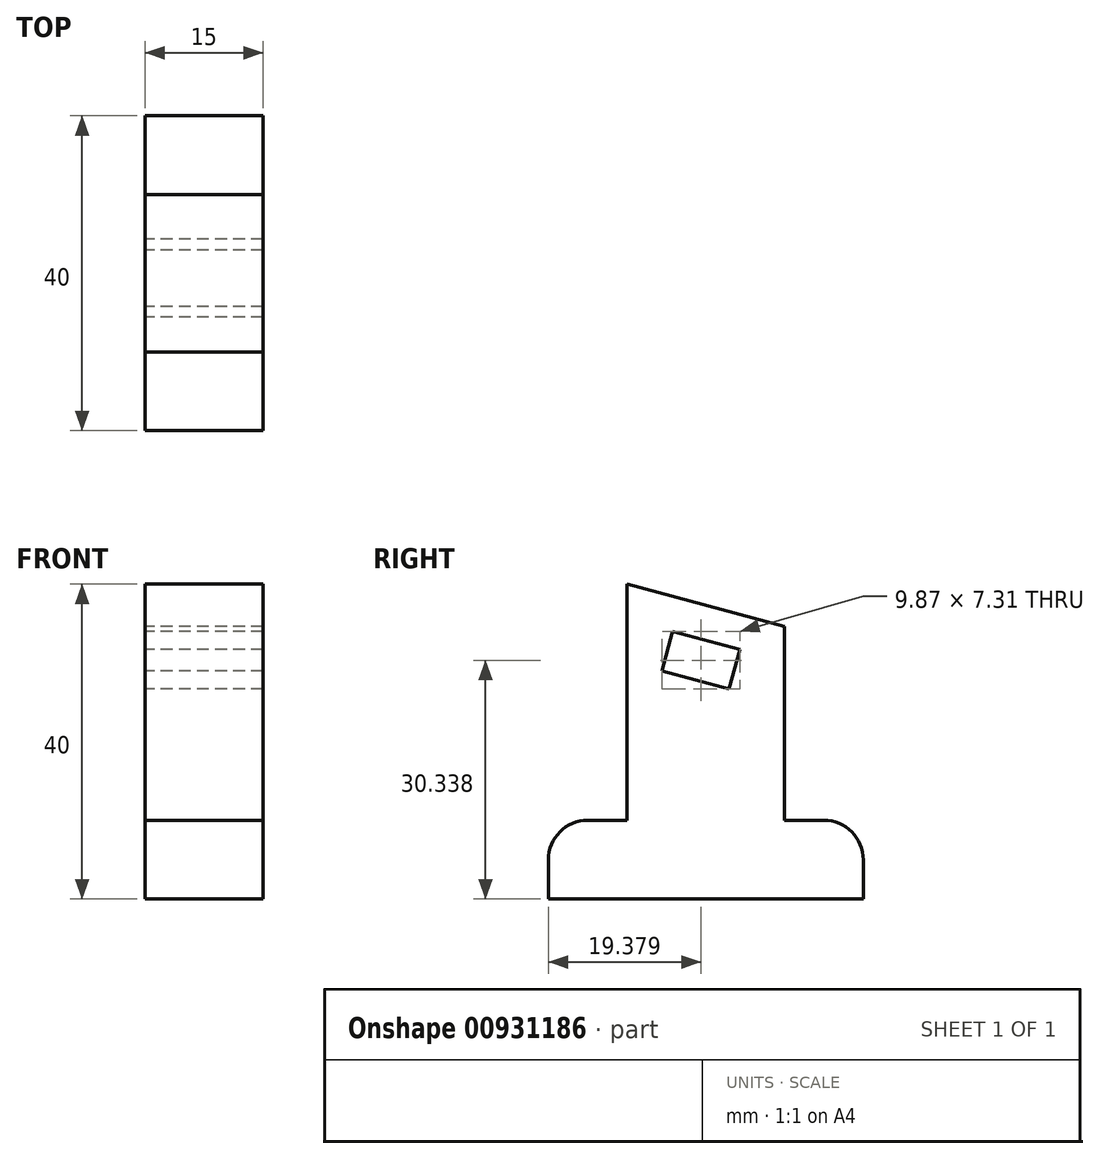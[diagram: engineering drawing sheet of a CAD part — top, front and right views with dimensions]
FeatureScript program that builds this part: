
annotation { "Feature Type Name" : "Feature", "Feature Type Description" : "" }
export const myFeature = defineFeature(function(context is Context, id is Id, definition is map)
    precondition{}
    {
        {
            var Q0;
            Q0=qCreatedBy(makeId("Right.planeOp"),FACE);
            var sketch = newSketch(context, id + "F0", { "sketchPlane" : qUnion([Q0])});
            skLineSegment(sketch, "E0.top", {"start": v(-10, -20) * mm, "end": v(10, -20) * mm});
            skLineSegment(sketch, "E0.left", {"start": v(-10, 20) * mm, "end": v(-10, -10) * mm});
            skLineSegment(sketch, "E0.right", {"start": v(10, 14.64) * mm, "end": v(10, -10) * mm});
            skPoint(sketch, "E0.middle", {"position": v(0, 0) * mm});
            skLineSegment(sketch, "E1.bottom", {"start": v(10, -20) * mm, "end": v(20, -20) * mm});
            skLineSegment(sketch, "E1.top", {"start": v(10, -10) * mm, "end": v(15, -10) * mm});
            skLineSegment(sketch, "E1.right", {"start": v(20, -20) * mm, "end": v(20, -15) * mm});
            skLineSegment(sketch, "E2.MirrorCS", {"start": v(-20, -20) * mm, "end": v(-20, -15) * mm});
            skLineSegment(sketch, "E3.MirrorCS", {"start": v(-10, -20) * mm, "end": v(-20, -20) * mm});
            skLineSegment(sketch, "E4.MirrorCS", {"start": v(-10, -10) * mm, "end": v(-15, -10) * mm});
            skPoint(sketch, "E5.orphan", {"position": v(0, -20) * mm});
            skPoint(sketch, "E6.start.orphan", {"position": v(0, 20) * mm});
            skLineSegment(sketch, "E7", {"start": v(-10, 20) * mm, "end": v(10, 14.64) * mm});
            skPoint(sketch, "E8.orphan", {"position": v(10, 20) * mm});
            skLineSegment(sketch, "E9", {"start": v(4.31, 11.7) * mm, "end": v(-4.21, 14) * mm});
            skLineSegment(sketch, "E10", {"start": v(-4.21, 14) * mm, "end": v(-5.56, 8.97) * mm});
            skLineSegment(sketch, "E11", {"start": v(-5.56, 8.97) * mm, "end": v(2.97, 6.68) * mm});
            skLineSegment(sketch, "E12", {"start": v(2.97, 6.68) * mm, "end": v(4.31, 11.7) * mm});
            skPoint(sketch, "E13.visualSharp", {"position": v(-20, -10) * mm});
            skArc(sketch, "E13.filletArc", {"start": v(-15, -10) * mm, "mid": v(-18.54, -11.46) * mm, "end": v(-20, -15) * mm});
            skPoint(sketch, "E14.visualSharp", {"position": v(20, -10) * mm});
            skArc(sketch, "E14.filletArc", {"start": v(20, -15) * mm, "mid": v(18.54, -11.46) * mm, "end": v(15, -10) * mm});
            skLineSegment(sketch, "E15", {"start": v(-10, 20) * mm, "end": v(10, 20) * mm, "construction": true});
            skLineSegment(sketch, "E16", {"start": v(10, 14.64) * mm, "end": v(10, 20) * mm, "construction": true});
            skSolve(sketch);
        }
        {
            var Q0;
            Q0 = qSketchRegion(id + "F0", true);
            extrude(context, id + "F1", {"entities" : qUnion([Q0]), "depth" : 15 * mm, "offsetDistance" : 25 * mm});
        }
    });
